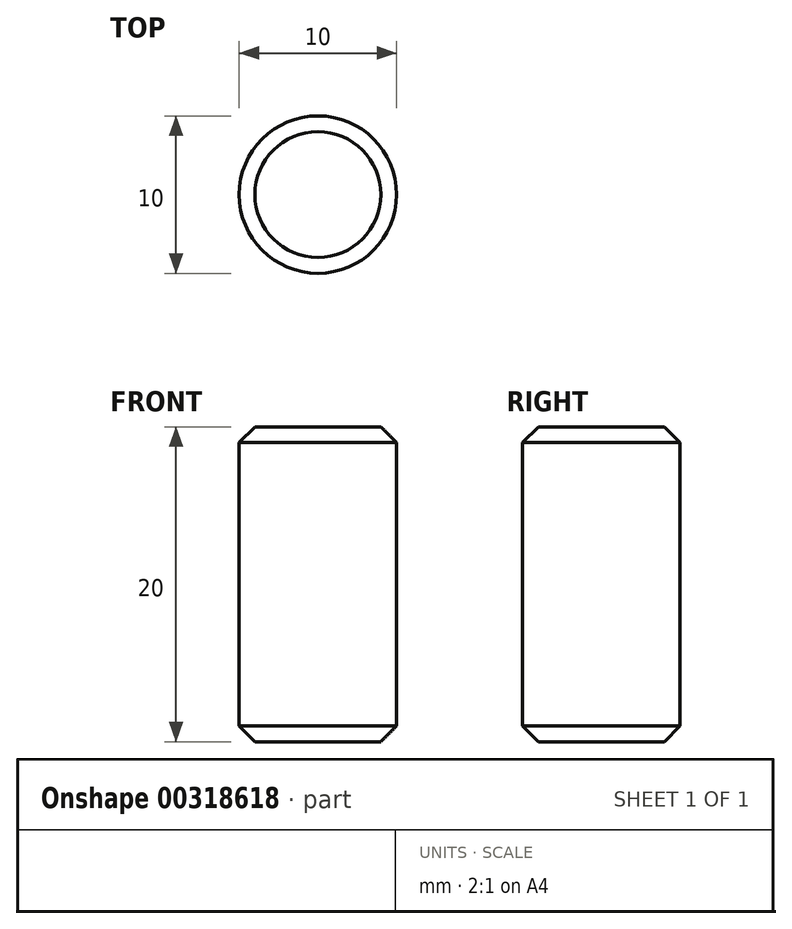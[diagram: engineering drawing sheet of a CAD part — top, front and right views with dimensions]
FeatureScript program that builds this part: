
annotation { "Feature Type Name" : "Feature", "Feature Type Description" : "" }
export const myFeature = defineFeature(function(context is Context, id is Id, definition is map)
    precondition{}
    {
        {
            var Q0;
            Q0=qCreatedBy(makeId("Top.planeOp"),FACE);
            var sketch = newSketch(context, id + "F0", { "sketchPlane" : qUnion([Q0])});
            skCircle(sketch, "E0", {"center": v(0, 0) * mm, "radius": 5 * mm});
            skSolve(sketch);
        }
        {
            var Q0;
            Q0=qSketchRegion(id+"F0",true);
            extrude(context, id + "F1", {"entities" : qUnion([Q0]), "endBound" : BoundingType.SYMMETRIC, "depth" : 20 * mm});
        }
        {
            var Q0;
            Q0=makeQuery(id+"F1.opExtrude","CAP_EDGE",EDGE,{"disambiguationData":[OSD([sQuery(id+"F0.wireOp",EDGE,"E0")])],"isStart":false});
            var Q1;
            Q1=makeQuery(id+"F1.opExtrude","CAP_EDGE",EDGE,{"disambiguationData":[OSD([sQuery(id+"F0.wireOp",EDGE,"E0")])],"isStart":true});
            chamfer(context, id + "F2", {"entities" : qUnion([Q0, Q1]), "width" : 1 * mm, "tangentPropagation" : true});
        }
    });
